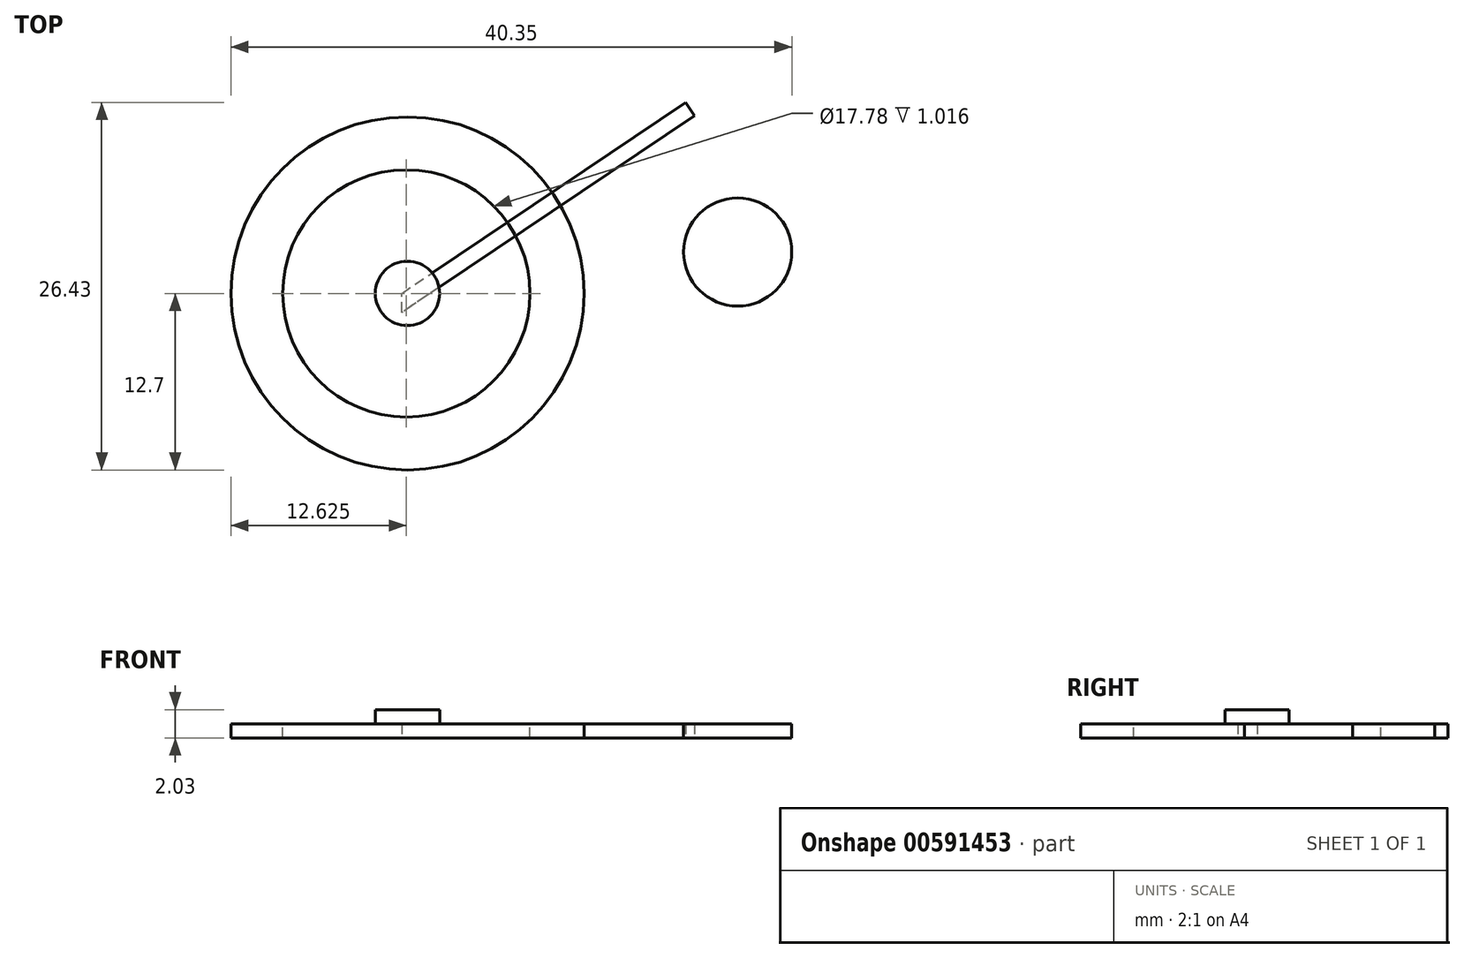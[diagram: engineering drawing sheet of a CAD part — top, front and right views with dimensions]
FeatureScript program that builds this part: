
annotation { "Feature Type Name" : "Feature", "Feature Type Description" : "" }
export const myFeature = defineFeature(function(context is Context, id is Id, definition is map)
    precondition{}
    {
        {
            var Q0;
            Q0=qCreatedBy(makeId("Top.planeOp"),FACE);
            var sketch = newSketch(context, id + "F0", { "sketchPlane" : qUnion([Q0])});
            skCircle(sketch, "E0", {"center": v(-17.42, 0) * mm, "radius": 12.7 * mm});
            skSolve(sketch);
        }
        {
            var Q0;
            Q0=makeQuery(id+"F0.imprint","IMPRINT",FACE,{"disambiguationData":[TD([[makeQuery(id+"F0.imprint","IMPRINT",EDGE,{"derivedFrom":sQuery(id+"F0.wireOp",EDGE,"E0")}),1.0]])]});
            extrude(context, id + "F1", {"entities" : qUnion([Q0]), "depth" : 1.02 * mm, "offsetDistance" : 25.4 * mm});
        }
        {
            var Q0;
            Q0=makeQuery(id+"F1.opExtrude","CAP_FACE",FACE,{"disambiguationData":[OSD([sQuery(id+"F0.wireOp",EDGE,"E0")])],"isStart":false});
            var sketch = newSketch(context, id + "F2", { "sketchPlane" : qUnion([Q0])});
            skCircle(sketch, "E1", {"center": v(-17.42, 0) * mm, "radius": 2.31 * mm});
            skSolve(sketch);
        }
        {
            var Q0;
            Q0=makeQuery(id+"F2.imprint","IMPRINT",FACE,{"disambiguationData":[TD([[makeQuery(id+"F2.imprint","IMPRINT",EDGE,{"derivedFrom":sQuery(id+"F2.wireOp",EDGE,"E1")}),-1.0]])]});
            var sketch = newSketch(context, id + "F3", { "sketchPlane" : qUnion([Q0])});
            skCircle(sketch, "E2", {"center": v(-17.5, 0) * mm, "radius": 9.45 * mm});
            skSolve(sketch);
        }
        {
            var Q0;
            Q0=sQuery(id+"F3.wireOp",VERTEX,"E2.center");
            var Q1;
            Q1=makeQuery(id+"F1.opExtrude","SWEPT_BODY",BODY,{"disambiguationData":[OSD([sQuery(id+"F0.wireOp",EDGE,"E0")])]});
            hole(context, id + "F4", {"style" : HoleStyle.SIMPLE, "endStyle" : HoleEndStyle.THROUGH, "holeDiameter" : 17.78 * mm, "majorDiameter" : 6.35 * mm, "isTappedThrough" : true, "tappedDepth" : 12.7 * mm, "tapClearance" : 3, "locations" : qUnion([Q0]), "scope" : qUnion([Q1])});
        }
        {
            var Q0;
            Q0=makeQuery(id+"F2.imprint","IMPRINT",FACE,{"disambiguationData":[TD([[makeQuery(id+"F2.imprint","IMPRINT",EDGE,{"derivedFrom":sQuery(id+"F2.wireOp",EDGE,"E1")}),1.0]])]});
            extrude(context, id + "F5", {"entities" : qUnion([Q0]), "depth" : 1.02 * mm, "offsetDistance" : 25.4 * mm});
        }
        {
            var Q0;
            Q0=qCreatedBy(makeId("Top.planeOp"),FACE);
            var sketch = newSketch(context, id + "F6", { "sketchPlane" : qUnion([Q0])});
            skCircle(sketch, "E3", {"center": v(6.34, 2.98) * mm, "radius": 3.89 * mm});
            skSolve(sketch);
        }
        {
            var Q0;
            Q0=makeQuery(id+"F6.imprint","IMPRINT",FACE,{"disambiguationData":[TD([[makeQuery(id+"F6.imprint","IMPRINT",EDGE,{"derivedFrom":sQuery(id+"F6.wireOp",EDGE,"E3")}),1.0]])]});
            extrude(context, id + "F7", {"entities" : qUnion([Q0]), "depth" : 1.02 * mm, "offsetDistance" : 25.4 * mm});
        }
        {
            var Q0;
            Q0=qCreatedBy(makeId("Top.planeOp"),FACE);
            var sketch = newSketch(context, id + "F8", { "sketchPlane" : qUnion([Q0])});
            skLineSegment(sketch, "E4", {"start": v(-17.83, 0) * mm, "end": v(2.59, 13.73) * mm});
            skLineSegment(sketch, "E5", {"start": v(2.59, 13.73) * mm, "end": v(3.23, 12.78) * mm});
            skLineSegment(sketch, "E6", {"start": v(3.23, 12.78) * mm, "end": v(-17.83, -1.38) * mm});
            skLineSegment(sketch, "E7", {"start": v(-17.83, -1.38) * mm, "end": v(-17.83, 0) * mm});
            skSolve(sketch);
        }
        {
            var Q0;
            Q0=makeQuery(id+"F8.imprint","IMPRINT",FACE,{"disambiguationData":[TD([[makeQuery(id+"F8.imprint","IMPRINT",EDGE,{"derivedFrom":sQuery(id+"F8.wireOp",EDGE,"E4")}),-1.0]])]});
            extrude(context, id + "F9", {"entities" : qUnion([Q0]), "depth" : 1.02 * mm, "offsetDistance" : 25.4 * mm});
        }
    });
